# Revit family: Dryer_Weight-Rated_Milnor_M96-Gas
name_source: partatom
category: Mechanical Equipment
units: mm (PartAtom-declared; Revit-internal decimal feet)

## family parameters
Always vertical = No
Classification Number = 23.45.70.11.14.17
Cut with Voids When Loaded = No
Maintain Annotation Orientation = No
Part Type = Normal
Room Calculation Point = No
Round Connector Dimension = Use Radius
Shared = No
Work Plane-Based = Yes

## types (8) — shared parameters
Assembly Code = E1010610
Capacity = 95 lbs Dry Weight
Circuit Breaker Size = 15 A
Cylinder Depth = 2' - 4 7/8"
Cylinder Diameter = 3' - 5 3/8"
Cylinder Volume = 22.5 CF
Default Elevation = 0' - 0"
Description = Milnor Commercial Laundry Dryer - Gas Model M96 as Specified
Door Base from FF = 2' - 0 1/2"
Door Opening = 2' - 7 3/8"
Door Opening Depth = 3' - 1 7/8"
Door Thickness = 0' - 1"
Electrical CL from CL = 0' - 7"
Electrical CL from FF = 6' - 2 5/16"
Electrical CL from Side = 0' - 3 1/4"
Exhaust CL from FF = 0' - 9 15/16"
Exhaust CL from Side = 1' - 1 1/4"
Exhaust Diameter = 1' - 4"
FSS Water Connection CL from FF = 5' - 7 3/8"
FSS Water Connection Diameter = 0' - 0 3/4"
FSS Water Connection from Side = 0' - 8 3/4"
Gas Connection CL from FF = 5' - 10 5/16"
Gas Connection Diameter = 0' - 1"
Gas Connection from Side = 1' - 2 3/8"
Heat Input = 350000.0 Btu/h
Keynote = 11110
Manufacturer = Pellerin Milnor Corp
Manufacturer Fax = 504-468-3094
Manufacturer Website = http://www.milnor.com
Model = M96
Number of Poles = 1
Phase = 3
Product Data = http://www.arcat.com
Reversing = Yes
Revision = R1_04-2011
Sales Information = http://www.milnor.com
Send Message = http://www.arcat.com
URL = http://www.milnor.com
Unit Depth = 2' - 10 1/4"
Unit Height = 6' - 10 3/8"
Unit Weight = 1087
Unit Width = 3' - 10 1/8"
exhaustrad = 0' - 8"
fsswaterrad = 0' - 0 3/8"
gasrad = 0' - 0 1/2"
zero-valued in all types: Expected Lifespan (Years), Maintenance Schedule (Months), Warranty Duration (Years)

## per-type parameters (varying)
| type | Air Flow | Frequency | MEP Amperage | Number of Wires | Voltage_MEP |
| 416-50-3ph 15A CB | 2250 CFM | 50 Hz | 5 A | 4 | 416 V |
| 400-50-3ph 15A CB | 2250 CFM | 50 Hz | 5 A | 4 | 400 V |
| 380-50-3ph 15A CB | 2250 CFM | 50 Hz | 6 A | 4 | 380 V |
| 240-50-3ph 15A CB | 2250 CFM | 50 Hz | 8 A | 3 | 230 V |
| 480-60-3ph 15A CB | 2700 CFM | 60 Hz | 6 A | 3 | 480 V |
| 460-60-3ph 15A CB | 2700 CFM | 60 Hz | 6 A | 3 | 460 V |
| 240-60-3ph 15A CB | 2700 CFM | 60 Hz | 10 A | 3 | 240 V |
| 208-60-3ph 15A CB | 2700 CFM | 60 Hz | 12 A | 3 | 208 V |

## geometry (parser evidence)
native form markers: Sweep x2
no freeform markers — native parametric forms only
